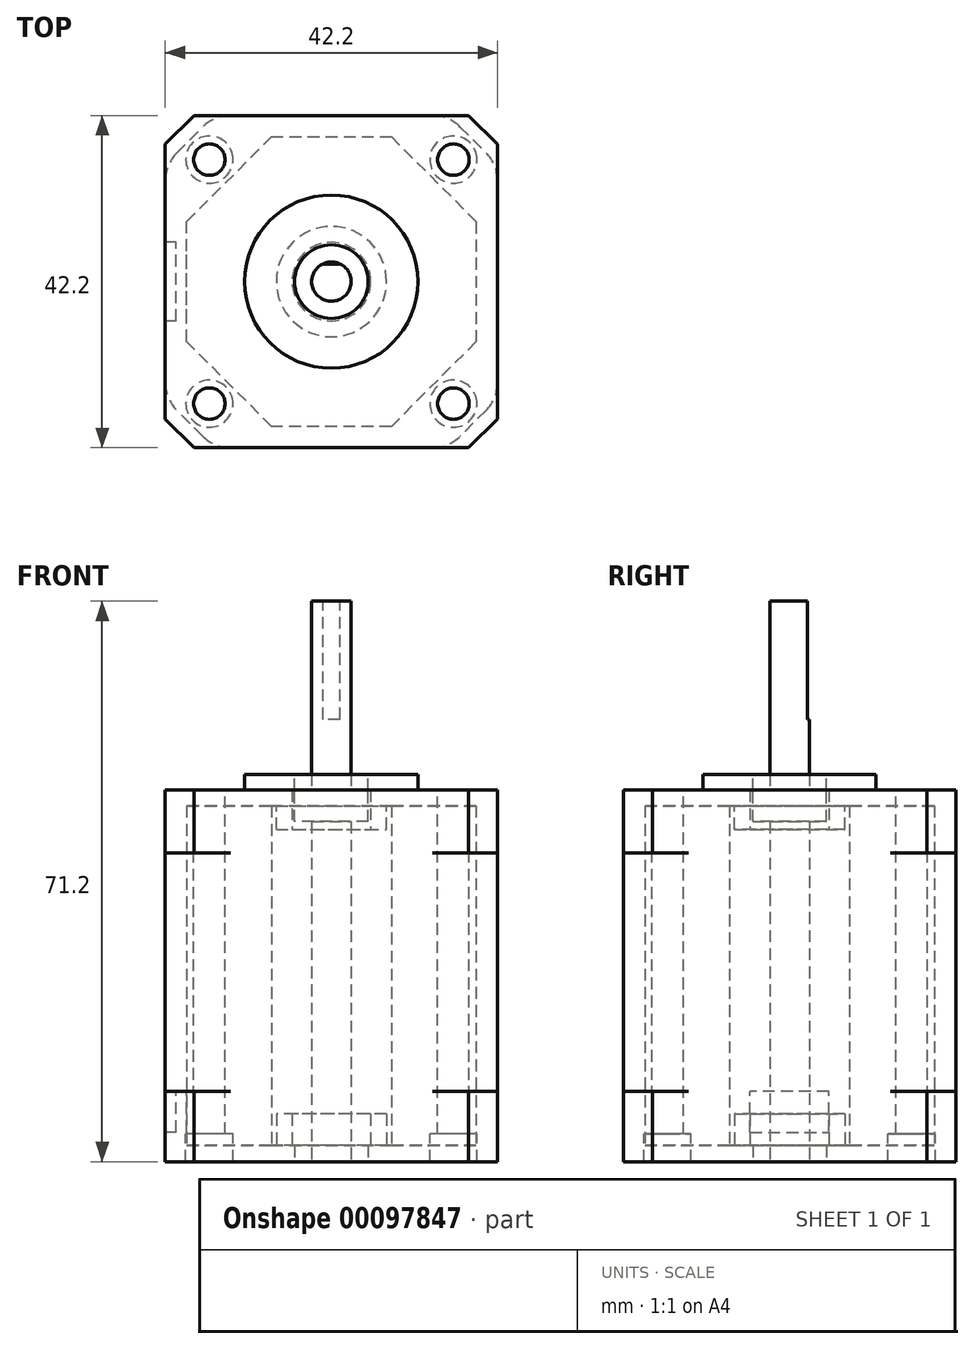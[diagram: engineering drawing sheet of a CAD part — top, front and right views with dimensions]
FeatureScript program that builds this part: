
annotation { "Feature Type Name" : "Feature", "Feature Type Description" : "" }
export const myFeature = defineFeature(function(context is Context, id is Id, definition is map)
    precondition{}
    {
        {
            var Q0;
            Q0=qCreatedBy(makeId("Top.planeOp"),FACE);
            var sketch = newSketch(context, id + "F0", { "sketchPlane" : qUnion([Q0])});
            skLineSegment(sketch, "E0.bottom", {"start": v(17.44, 21.1) * mm, "end": v(-17.44, 21.1) * mm});
            skLineSegment(sketch, "E0.top", {"start": v(17.44, -21.1) * mm, "end": v(-17.44, -21.1) * mm});
            skLineSegment(sketch, "E0.left", {"start": v(21.1, 17.44) * mm, "end": v(21.1, -17.44) * mm});
            skLineSegment(sketch, "E0.right", {"start": v(-21.1, 17.44) * mm, "end": v(-21.1, -17.44) * mm});
            skPoint(sketch, "E0.middle", {"position": v(0, 0) * mm});
            skLineSegment(sketch, "E1.bottom", {"start": v(15.5, 15.5) * mm, "end": v(-15.5, 15.5) * mm, "construction": true});
            skLineSegment(sketch, "E1.top", {"start": v(15.5, -15.5) * mm, "end": v(-15.5, -15.5) * mm, "construction": true});
            skLineSegment(sketch, "E1.left", {"start": v(15.5, 15.5) * mm, "end": v(15.5, -15.5) * mm, "construction": true});
            skLineSegment(sketch, "E1.right", {"start": v(-15.5, 15.5) * mm, "end": v(-15.5, -15.5) * mm, "construction": true});
            skCircle(sketch, "E2", {"center": v(-15.5, 15.5) * mm, "radius": 2 * mm});
            skCircle(sketch, "E3", {"center": v(15.5, 15.5) * mm, "radius": 2 * mm});
            skCircle(sketch, "E4", {"center": v(-15.5, -15.5) * mm, "radius": 2 * mm});
            skCircle(sketch, "E5", {"center": v(15.5, -15.5) * mm, "radius": 2 * mm});
            skLineSegment(sketch, "E6.1", {"start": v(-21.1, 17.44) * mm, "end": v(-17.44, 21.1) * mm});
            skLineSegment(sketch, "E7", {"start": v(0, 21.1) * mm, "end": v(0, -21.1) * mm, "construction": true});
            skLineSegment(sketch, "E8", {"start": v(-21.1, 0) * mm, "end": v(21.1, 0) * mm, "construction": true});
            skLineSegment(sketch, "E9.MirrorCS", {"start": v(21.1, 17.44) * mm, "end": v(17.44, 21.1) * mm});
            skLineSegment(sketch, "E10.MirrorCS", {"start": v(-21.1, -17.44) * mm, "end": v(-17.44, -21.1) * mm});
            skLineSegment(sketch, "E11.MirrorCS", {"start": v(21.1, -17.44) * mm, "end": v(17.44, -21.1) * mm});
            skCircle(sketch, "E12", {"center": v(0, 0) * mm, "radius": 4.68 * mm});
            skCircle(sketch, "E13", {"center": v(0, 0) * mm, "radius": 2.5 * mm});
            skCircle(sketch, "E14", {"center": v(0, 0) * mm, "radius": 11 * mm});
            skSolve(sketch);
        }
        {
            var Q0;
            Q0=makeQuery(id+"F0.imprint","IMPRINT",FACE,{"disambiguationData":[TD([[makeQuery(id+"F0.imprint","IMPRINT",EDGE,{"derivedFrom":sQuery(id+"F0.wireOp",EDGE,"E0.bottom")}),1.0]])]});
            var Q1;
            Q1=makeQuery(id+"F0.imprint","IMPRINT",FACE,{"disambiguationData":[TD([[makeQuery(id+"F0.imprint","IMPRINT",EDGE,{"derivedFrom":sQuery(id+"F0.wireOp",EDGE,"E12")}),-1.0]])]});
            extrude(context, id + "F1", {"entities" : qUnion([Q0, Q1]), "oppositeDirection" : true, "depth" : 8 * mm});
        }
        {
            var Q0;
            Q0=makeQuery(id+"F0.imprint","IMPRINT",FACE,{"disambiguationData":[TD([[makeQuery(id+"F0.imprint","IMPRINT",EDGE,{"derivedFrom":sQuery(id+"F0.wireOp",EDGE,"E12")}),-1.0]])]});
            extrude(context, id + "F2", {"entities" : qUnion([Q0]), "operationType" : NewBodyOperationType.ADD, "depth" : 2 * mm});
        }
        {
            var Q0;
            Q0=makeQuery(id+"F1.opExtrude","CAP_FACE",FACE,{"disambiguationData":[OSD([sQuery(id+"F0.wireOp",EDGE,"E0.bottom"),sQuery(id+"F0.wireOp",EDGE,"E0.top"),sQuery(id+"F0.wireOp",EDGE,"E0.left"),sQuery(id+"F0.wireOp",EDGE,"E0.right"),sQuery(id+"F0.wireOp",EDGE,"E2"),sQuery(id+"F0.wireOp",EDGE,"E3"),sQuery(id+"F0.wireOp",EDGE,"E4"),sQuery(id+"F0.wireOp",EDGE,"E5"),sQuery(id+"F0.wireOp",EDGE,"E6.1"),sQuery(id+"F0.wireOp",EDGE,"E9.MirrorCS"),sQuery(id+"F0.wireOp",EDGE,"E10.MirrorCS"),sQuery(id+"F0.wireOp",EDGE,"E11.MirrorCS"),sQuery(id+"F0.wireOp",EDGE,"E12")])],"isStart":true});
            cPlane(context, id + "F3", {"entities" : qUnion([Q0]), "cplaneType" : CPlaneType.OFFSET, "offset" : (47.2 - 3.5) * mm, "oppositeDirection" : true, "width" : 150 * mm, "height" : 150 * mm});
        }
        {
            var Q0;
            Q0=qCreatedBy(id+"F3.planeOp",FACE);
            var sketch = newSketch(context, id + "F4", { "sketchPlane" : qUnion([Q0])});
            skLineSegment(sketch, "E15.0", {"start": v(17.44, 21.1) * mm, "end": v(-17.44, 21.1) * mm});
            skLineSegment(sketch, "E15.1", {"start": v(17.44, -21.1) * mm, "end": v(-17.44, -21.1) * mm});
            skLineSegment(sketch, "E15.2", {"start": v(21.1, 17.44) * mm, "end": v(21.1, -17.44) * mm});
            skLineSegment(sketch, "E15.3", {"start": v(-21.1, 17.44) * mm, "end": v(-21.1, -17.44) * mm});
            skPoint(sketch, "E15.4", {"position": v(0, 0) * mm});
            skLineSegment(sketch, "E15.5", {"start": v(15.5, 15.5) * mm, "end": v(-15.5, 15.5) * mm, "construction": true});
            skLineSegment(sketch, "E15.6", {"start": v(15.5, -15.5) * mm, "end": v(-15.5, -15.5) * mm, "construction": true});
            skLineSegment(sketch, "E15.7", {"start": v(15.5, 15.5) * mm, "end": v(15.5, -15.5) * mm, "construction": true});
            skLineSegment(sketch, "E15.8", {"start": v(-15.5, 15.5) * mm, "end": v(-15.5, -15.5) * mm, "construction": true});
            skPoint(sketch, "E15.9", {"position": v(0, 0) * mm});
            skCircle(sketch, "E15.10", {"center": v(-15.5, 15.5) * mm, "radius": 2 * mm});
            skCircle(sketch, "E15.11", {"center": v(15.5, 15.5) * mm, "radius": 2 * mm});
            skCircle(sketch, "E15.12", {"center": v(-15.5, -15.5) * mm, "radius": 2 * mm});
            skCircle(sketch, "E15.13", {"center": v(15.5, -15.5) * mm, "radius": 2 * mm});
            skLineSegment(sketch, "E15.14", {"start": v(-21.1, 17.44) * mm, "end": v(-17.44, 21.1) * mm});
            skLineSegment(sketch, "E15.15", {"start": v(0, 21.1) * mm, "end": v(0, -21.1) * mm, "construction": true});
            skLineSegment(sketch, "E15.16", {"start": v(-21.1, 0) * mm, "end": v(21.1, 0) * mm, "construction": true});
            skLineSegment(sketch, "E15.17", {"start": v(21.1, 17.44) * mm, "end": v(17.44, 21.1) * mm});
            skLineSegment(sketch, "E15.18", {"start": v(-21.1, -17.44) * mm, "end": v(-17.44, -21.1) * mm});
            skLineSegment(sketch, "E15.19", {"start": v(21.1, -17.44) * mm, "end": v(17.44, -21.1) * mm});
            skCircle(sketch, "E15.20", {"center": v(0, 0) * mm, "radius": 4.68 * mm});
            skCircle(sketch, "E15.21", {"center": v(0, 0) * mm, "radius": 2.5 * mm});
            skCircle(sketch, "E16", {"center": v(15.5, 15.5) * mm, "radius": 3 * mm});
            skCircle(sketch, "E17.MirrorC", {"center": v(-15.5, 15.5) * mm, "radius": 3 * mm});
            skCircle(sketch, "E18.MirrorC", {"center": v(-15.5, -15.5) * mm, "radius": 3 * mm});
            skCircle(sketch, "E19.MirrorC", {"center": v(15.5, -15.5) * mm, "radius": 3 * mm});
            skSolve(sketch);
        }
        {
            var Q0;
            Q0=makeQuery(id+"F4.imprint","IMPRINT",FACE,{"disambiguationData":[TD([[makeQuery(id+"F4.imprint","IMPRINT",EDGE,{"derivedFrom":sQuery(id+"F4.wireOp",EDGE,"E15.0")}),1.0]])]});
            var Q1;
            Q1=makeQuery(id+"F4.imprint","IMPRINT",FACE,{"disambiguationData":[TD([[makeQuery(id+"F4.imprint","IMPRINT",EDGE,{"derivedFrom":sQuery(id+"F4.wireOp",EDGE,"E15.11")}),-1.0]])]});
            var Q2;
            Q2=makeQuery(id+"F4.imprint","IMPRINT",FACE,{"disambiguationData":[TD([[makeQuery(id+"F4.imprint","IMPRINT",EDGE,{"derivedFrom":sQuery(id+"F4.wireOp",EDGE,"E15.10")}),-1.0]])]});
            var Q3;
            Q3=makeQuery(id+"F4.imprint","IMPRINT",FACE,{"disambiguationData":[TD([[makeQuery(id+"F4.imprint","IMPRINT",EDGE,{"derivedFrom":sQuery(id+"F4.wireOp",EDGE,"E15.12")}),-1.0]])]});
            var Q4;
            Q4=makeQuery(id+"F4.imprint","IMPRINT",FACE,{"disambiguationData":[TD([[makeQuery(id+"F4.imprint","IMPRINT",EDGE,{"derivedFrom":sQuery(id+"F4.wireOp",EDGE,"E15.13")}),-1.0]])]});
            extrude(context, id + "F5", {"entities" : qUnion([Q0, Q1, Q2, Q3, Q4]), "depth" : (8.9 - 3.5) * mm});
        }
        {
            var Q0;
            Q0=makeQuery(id+"F4.imprint","IMPRINT",FACE,{"disambiguationData":[TD([[makeQuery(id+"F4.imprint","IMPRINT",EDGE,{"derivedFrom":sQuery(id+"F4.wireOp",EDGE,"E15.0")}),1.0]])]});
            extrude(context, id + "F6", {"entities" : qUnion([Q0]), "operationType" : NewBodyOperationType.ADD, "oppositeDirection" : true, "depth" : 3.5 * mm});
        }
        {
            var Q0;
            Q0=makeQuery(id+"F5.opExtrude","CAP_FACE",FACE,{"disambiguationData":[OSD([sQuery(id+"F4.wireOp",EDGE,"E15.0"),sQuery(id+"F4.wireOp",EDGE,"E15.1"),sQuery(id+"F4.wireOp",EDGE,"E15.2"),sQuery(id+"F4.wireOp",EDGE,"E15.3"),sQuery(id+"F4.wireOp",EDGE,"E15.10"),sQuery(id+"F4.wireOp",EDGE,"E15.11"),sQuery(id+"F4.wireOp",EDGE,"E15.12"),sQuery(id+"F4.wireOp",EDGE,"E15.13"),sQuery(id+"F4.wireOp",EDGE,"E15.14"),sQuery(id+"F4.wireOp",EDGE,"E15.17"),sQuery(id+"F4.wireOp",EDGE,"E15.18"),sQuery(id+"F4.wireOp",EDGE,"E15.19"),sQuery(id+"F4.wireOp",EDGE,"E15.20")])],"isStart":false});
            var sketch = newSketch(context, id + "F7", { "sketchPlane" : qUnion([Q0])});
            skLineSegment(sketch, "E20.1", {"start": v(16.7, -19.3) * mm, "end": v(19.3, -16.7) * mm});
            skLineSegment(sketch, "E20.2", {"start": v(19.3, 16.7) * mm, "end": v(16.7, 19.3) * mm});
            skLineSegment(sketch, "E20.5", {"start": v(-16.69, 19.3) * mm, "end": v(-19.3, 16.7) * mm});
            skLineSegment(sketch, "E20.7", {"start": v(-19.3, -16.7) * mm, "end": v(-16.7, -19.3) * mm});
            skLineSegment(sketch, "E21.0", {"start": v(-19.64, 16.36) * mm, "end": v(-19.3, 16.7) * mm});
            skLineSegment(sketch, "E21.2", {"start": v(16.36, 19.64) * mm, "end": v(16.7, 19.3) * mm});
            skLineSegment(sketch, "E21.4", {"start": v(19.64, -16.36) * mm, "end": v(19.3, -16.7) * mm});
            skLineSegment(sketch, "E21.6", {"start": v(-16.36, -19.64) * mm, "end": v(-19.64, -16.36) * mm});
            skLineSegment(sketch, "E22.0", {"start": v(-21.1, 12.82) * mm, "end": v(-21.1, -12.82) * mm});
            skLineSegment(sketch, "E22.1", {"start": v(-21.1, 17.44) * mm, "end": v(-17.44, 21.1) * mm});
            skLineSegment(sketch, "E22.2", {"start": v(12.82, 21.1) * mm, "end": v(-12.82, 21.1) * mm});
            skLineSegment(sketch, "E22.3", {"start": v(21.1, 17.44) * mm, "end": v(17.44, 21.1) * mm});
            skLineSegment(sketch, "E22.4", {"start": v(21.1, 12.82) * mm, "end": v(21.1, -12.82) * mm});
            skLineSegment(sketch, "E22.5", {"start": v(21.1, -17.44) * mm, "end": v(17.44, -21.1) * mm});
            skLineSegment(sketch, "E22.6", {"start": v(12.82, -21.1) * mm, "end": v(-12.82, -21.1) * mm});
            skLineSegment(sketch, "E22.7", {"start": v(-21.1, -17.44) * mm, "end": v(-17.44, -21.1) * mm});
            skPoint(sketch, "E23.orphan", {"position": v(-10.54, 25.45) * mm});
            skLineSegment(sketch, "E24.trimOffspring", {"start": v(16.7, -19.3) * mm, "end": v(16.36, -19.64) * mm});
            skLineSegment(sketch, "E25.trimOffspring", {"start": v(19.3, 16.7) * mm, "end": v(19.64, 16.36) * mm});
            skLineSegment(sketch, "E26.trimOffspring", {"start": v(-16.69, 19.3) * mm, "end": v(-16.36, 19.64) * mm});
            skCircle(sketch, "E27.cCircle", {"center": v(0, 0) * mm, "radius": 18.4 * mm, "construction": true});
            skLineSegment(sketch, "E27.0", {"start": v(-18.4, 7.61) * mm, "end": v(-7.62, 18.39) * mm});
            skLineSegment(sketch, "E27.1", {"start": v(-7.62, 18.39) * mm, "end": v(7.61, 18.4) * mm});
            skLineSegment(sketch, "E27.2", {"start": v(7.61, 18.4) * mm, "end": v(18.39, 7.62) * mm});
            skLineSegment(sketch, "E27.3", {"start": v(18.39, 7.62) * mm, "end": v(18.4, -7.61) * mm});
            skLineSegment(sketch, "E27.4", {"start": v(18.4, -7.61) * mm, "end": v(7.62, -18.39) * mm});
            skLineSegment(sketch, "E27.5", {"start": v(7.62, -18.39) * mm, "end": v(-7.61, -18.4) * mm});
            skLineSegment(sketch, "E27.6", {"start": v(-7.61, -18.4) * mm, "end": v(-18.39, -7.62) * mm});
            skLineSegment(sketch, "E27.7", {"start": v(-18.39, -7.62) * mm, "end": v(-18.4, 7.61) * mm});
            skLineSegment(sketch, "E28", {"start": v(0, 21.1) * mm, "end": v(0, -21.1) * mm, "construction": true});
            skPoint(sketch, "E29.newPointA", {"position": v(17.44, 21.1) * mm});
            skArc(sketch, "E29.filletArc", {"start": v(16.36, 19.64) * mm, "mid": v(14.73, 20.72) * mm, "end": v(12.82, 21.1) * mm});
            skArc(sketch, "E30.filletArc", {"start": v(21.1, 12.82) * mm, "mid": v(20.72, 14.73) * mm, "end": v(19.64, 16.36) * mm});
            skPoint(sketch, "E31.newPointB", {"position": v(-21.1, 17.44) * mm});
            skArc(sketch, "E31.filletArc", {"start": v(-19.64, 16.36) * mm, "mid": v(-20.72, 14.73) * mm, "end": v(-21.1, 12.82) * mm});
            skPoint(sketch, "E32.newPointB", {"position": v(-17.44, 21.1) * mm});
            skArc(sketch, "E32.filletArc", {"start": v(-12.82, 21.1) * mm, "mid": v(-14.73, 20.72) * mm, "end": v(-16.36, 19.64) * mm});
            skPoint(sketch, "E33.newPointB", {"position": v(21.1, -17.44) * mm});
            skArc(sketch, "E33.filletArc", {"start": v(19.64, -16.36) * mm, "mid": v(20.72, -14.73) * mm, "end": v(21.1, -12.82) * mm});
            skArc(sketch, "E34.filletArc", {"start": v(12.82, -21.1) * mm, "mid": v(14.73, -20.72) * mm, "end": v(16.36, -19.64) * mm});
            skPoint(sketch, "E35.newPointA", {"position": v(-21.1, -17.44) * mm});
            skArc(sketch, "E35.filletArc", {"start": v(-21.1, -12.82) * mm, "mid": v(-20.72, -14.73) * mm, "end": v(-19.64, -16.36) * mm});
            skPoint(sketch, "E36.newPointB", {"position": v(-17.44, -21.1) * mm});
            skArc(sketch, "E36.filletArc", {"start": v(-16.36, -19.64) * mm, "mid": v(-14.73, -20.72) * mm, "end": v(-12.82, -21.1) * mm});
            skPoint(sketch, "E37.middle", {"position": v(-18.4, 0) * mm});
            skSolve(sketch);
        }
        {
            var Q0;
            Q0=makeQuery(id+"F7.imprint","IMPRINT",FACE,{"disambiguationData":[TD([[makeQuery(id+"F7.imprint","IMPRINT",EDGE,{"derivedFrom":sQuery(id+"F7.wireOp",EDGE,"E20.1")}),1.0]])]});
            extrude(context, id + "F8", {"entities" : qUnion([Q0]), "endBound" : BoundingType.UP_TO_NEXT, "depth" : 25 * mm});
        }
        {
            var Q0;
            Q0=makeQuery(id+"F0.imprint","IMPRINT",FACE,{"disambiguationData":[TD([[makeQuery(id+"F0.imprint","IMPRINT",EDGE,{"derivedFrom":sQuery(id+"F0.wireOp",EDGE,"E13")}),1.0]])]});
            extrude(context, id + "F9", {"entities" : qUnion([Q0]), "depth" : 24 * mm});
        }
        {
            var Q0;
            Q0=makeQuery(id+"F0.imprint","IMPRINT",FACE,{"disambiguationData":[TD([[makeQuery(id+"F0.imprint","IMPRINT",EDGE,{"derivedFrom":sQuery(id+"F0.wireOp",EDGE,"E13")}),1.0]])]});
            var Q1;
            Q1=makeQuery(id+"F6.opExtrude","CAP_FACE",FACE,{"disambiguationData":[OSD([sQuery(id+"F4.wireOp",EDGE,"E15.0"),sQuery(id+"F4.wireOp",EDGE,"E15.1"),sQuery(id+"F4.wireOp",EDGE,"E15.2"),sQuery(id+"F4.wireOp",EDGE,"E15.3"),sQuery(id+"F4.wireOp",EDGE,"E15.14"),sQuery(id+"F4.wireOp",EDGE,"E15.17"),sQuery(id+"F4.wireOp",EDGE,"E15.18"),sQuery(id+"F4.wireOp",EDGE,"E15.19"),sQuery(id+"F4.wireOp",EDGE,"E15.20"),sQuery(id+"F4.wireOp",EDGE,"E16"),sQuery(id+"F4.wireOp",EDGE,"E17.MirrorC"),sQuery(id+"F4.wireOp",EDGE,"E18.MirrorC"),sQuery(id+"F4.wireOp",EDGE,"E19.MirrorC")])],"isStart":false});
            extrude(context, id + "F10", {"entities" : qUnion([Q0]), "operationType" : NewBodyOperationType.ADD, "endBound" : BoundingType.UP_TO_SURFACE, "oppositeDirection" : true, "endBoundEntityFace" : qUnion([Q1]), "depth" : 25 * mm});
        }
        {
            var Q0;
            Q0=makeQuery(id+"F9.opExtrude","CAP_FACE",FACE,{"disambiguationData":[OSD([sQuery(id+"F0.wireOp",EDGE,"E13")])],"isStart":false});
            var sketch = newSketch(context, id + "F11", { "sketchPlane" : qUnion([Q0])});
            skLineSegment(sketch, "E38", {"start": v(0, 0) * mm, "end": v(0, 2.25) * mm, "construction": true});
            skLineSegment(sketch, "E39", {"start": v(0, 2.25) * mm, "end": v(-1.09, 2.25) * mm});
            skLineSegment(sketch, "E40.MirrorCS", {"start": v(0, 2.25) * mm, "end": v(1.09, 2.25) * mm});
            skCircle(sketch, "E41.0", {"center": v(0, 0) * mm, "radius": 2.5 * mm});
            skSolve(sketch);
        }
        {
            var Q0;
            {var subQ0=sQuery(id+"F11.wireOp",EDGE,"E39");Q0=makeQuery(id+"F11.imprint","IMPRINT",FACE,{"disambiguationData":[TD([[makeQuery(id+"F11.imprint","IMPRINT",EDGE,{"derivedFrom":subQ0}),-1.0]])]});}
            extrude(context, id + "F12", {"entities" : qUnion([Q0]), "operationType" : NewBodyOperationType.REMOVE, "oppositeDirection" : true, "depth" : 15 * mm});
        }
        {
            var Q0;
            Q0=makeQuery(id+"F7.imprint","IMPRINT",FACE,{"disambiguationData":[TD([[makeQuery(id+"F7.imprint","IMPRINT",EDGE,{"derivedFrom":sQuery(id+"F7.wireOp",EDGE,"E27.0")}),-1.0]])]});
            extrude(context, id + "F13", {"entities" : qUnion([Q0]), "operationType" : NewBodyOperationType.REMOVE, "oppositeDirection" : true, "depth" : (8.86 - 2) * mm});
        }
        {
            var Q0;
            Q0=makeQuery(id+"F1.opExtrude","CAP_FACE",FACE,{"disambiguationData":[OSD([sQuery(id+"F0.wireOp",EDGE,"E0.bottom"),sQuery(id+"F0.wireOp",EDGE,"E0.top"),sQuery(id+"F0.wireOp",EDGE,"E0.left"),sQuery(id+"F0.wireOp",EDGE,"E0.right"),sQuery(id+"F0.wireOp",EDGE,"E2"),sQuery(id+"F0.wireOp",EDGE,"E3"),sQuery(id+"F0.wireOp",EDGE,"E4"),sQuery(id+"F0.wireOp",EDGE,"E5"),sQuery(id+"F0.wireOp",EDGE,"E6.1"),sQuery(id+"F0.wireOp",EDGE,"E9.MirrorCS"),sQuery(id+"F0.wireOp",EDGE,"E10.MirrorCS"),sQuery(id+"F0.wireOp",EDGE,"E11.MirrorCS"),sQuery(id+"F0.wireOp",EDGE,"E12")])],"isStart":false});
            var sketch = newSketch(context, id + "F14", { "sketchPlane" : qUnion([Q0])});
            skLineSegment(sketch, "E42.0.0", {"start": v(-7.62, -18.39) * mm, "end": v(-18.4, -7.61) * mm});
            skLineSegment(sketch, "E42.0.1", {"start": v(-18.4, -7.61) * mm, "end": v(-18.39, 7.62) * mm});
            skLineSegment(sketch, "E42.0.2", {"start": v(-18.39, 7.62) * mm, "end": v(-7.61, 18.4) * mm});
            skLineSegment(sketch, "E42.0.3", {"start": v(-7.61, 18.4) * mm, "end": v(7.62, 18.39) * mm});
            skLineSegment(sketch, "E42.0.4", {"start": v(7.62, 18.39) * mm, "end": v(18.4, 7.61) * mm});
            skLineSegment(sketch, "E42.0.5", {"start": v(18.4, 7.61) * mm, "end": v(18.39, -7.62) * mm});
            skLineSegment(sketch, "E42.0.6", {"start": v(18.39, -7.62) * mm, "end": v(7.61, -18.4) * mm});
            skLineSegment(sketch, "E42.0.7", {"start": v(7.61, -18.4) * mm, "end": v(-7.62, -18.39) * mm});
            skSolve(sketch);
        }
        {
            var Q0;
            Q0=makeQuery(id+"F14.imprint","IMPRINT",FACE,{"disambiguationData":[TD([[makeQuery(id+"F14.imprint","IMPRINT",EDGE,{"derivedFrom":sQuery(id+"F14.wireOp",EDGE,"E42.0.0")}),-1.0]])]});
            extrude(context, id + "F15", {"entities" : qUnion([Q0]), "operationType" : NewBodyOperationType.REMOVE, "oppositeDirection" : true, "depth" : 6 * mm});
        }
        {
            var Q0;
            Q0=makeQuery(id+"F15.boolean.opBoolean","COPY",FACE,{"derivedFrom":makeQuery(id+"F15.opExtrude","CAP_FACE",FACE,{"disambiguationData":[OSD([sQuery(id+"F0.wireOp",EDGE,"E12"),sQuery(id+"F14.wireOp",EDGE,"E42.0.0"),sQuery(id+"F14.wireOp",EDGE,"E42.0.1"),sQuery(id+"F14.wireOp",EDGE,"E42.0.2"),sQuery(id+"F14.wireOp",EDGE,"E42.0.3"),sQuery(id+"F14.wireOp",EDGE,"E42.0.4"),sQuery(id+"F14.wireOp",EDGE,"E42.0.5"),sQuery(id+"F14.wireOp",EDGE,"E42.0.6"),sQuery(id+"F14.wireOp",EDGE,"E42.0.7")])],"isStart":false})});
            var sketch = newSketch(context, id + "F16", { "sketchPlane" : qUnion([Q0])});
            skCircle(sketch, "E43.0", {"center": v(0, 0) * mm, "radius": 4.68 * mm});
            skCircle(sketch, "E44", {"center": v(0, 0) * mm, "radius": 5 * mm});
            skCircle(sketch, "E45", {"center": v(0, 0) * mm, "radius": 7 * mm});
            skSolve(sketch);
        }
        {
            var Q0;
            Q0=makeQuery(id+"F16.imprint","IMPRINT",FACE,{"disambiguationData":[TD([[makeQuery(id+"F16.imprint","IMPRINT",EDGE,{"derivedFrom":sQuery(id+"F16.wireOp",EDGE,"E43.0")}),1.0]])]});
            extrude(context, id + "F17", {"entities" : qUnion([Q0]), "operationType" : NewBodyOperationType.REMOVE, "oppositeDirection" : true, "depth" : 2 * mm});
        }
        {
            var Q0;
            Q0=makeQuery(id+"F16.imprint","IMPRINT",FACE,{"disambiguationData":[TD([[makeQuery(id+"F16.imprint","IMPRINT",EDGE,{"derivedFrom":sQuery(id+"F16.wireOp",EDGE,"E44")}),-1.0]])]});
            var Q1;
            Q1=makeQuery(id+"F1.opExtrude","CAP_FACE",FACE,{"disambiguationData":[OSD([sQuery(id+"F0.wireOp",EDGE,"E0.bottom"),sQuery(id+"F0.wireOp",EDGE,"E0.top"),sQuery(id+"F0.wireOp",EDGE,"E0.left"),sQuery(id+"F0.wireOp",EDGE,"E0.right"),sQuery(id+"F0.wireOp",EDGE,"E2"),sQuery(id+"F0.wireOp",EDGE,"E3"),sQuery(id+"F0.wireOp",EDGE,"E4"),sQuery(id+"F0.wireOp",EDGE,"E5"),sQuery(id+"F0.wireOp",EDGE,"E6.1"),sQuery(id+"F0.wireOp",EDGE,"E9.MirrorCS"),sQuery(id+"F0.wireOp",EDGE,"E10.MirrorCS"),sQuery(id+"F0.wireOp",EDGE,"E11.MirrorCS"),sQuery(id+"F0.wireOp",EDGE,"E12")])],"isStart":false});
            extrude(context, id + "F18", {"entities" : qUnion([Q0]), "operationType" : NewBodyOperationType.ADD, "endBoundEntityFace" : qUnion([Q1]), "depth" : 3 * mm});
        }
        {
            var Q0;
            Q0=makeQuery(id+"F13.boolean.opBoolean","COPY",FACE,{"derivedFrom":makeQuery(id+"F13.opExtrude","CAP_FACE",FACE,{"disambiguationData":[OSD([sQuery(id+"F4.wireOp",EDGE,"E15.20"),sQuery(id+"F7.wireOp",EDGE,"E27.0"),sQuery(id+"F7.wireOp",EDGE,"E27.1"),sQuery(id+"F7.wireOp",EDGE,"E27.2"),sQuery(id+"F7.wireOp",EDGE,"E27.3"),sQuery(id+"F7.wireOp",EDGE,"E27.4"),sQuery(id+"F7.wireOp",EDGE,"E27.5"),sQuery(id+"F7.wireOp",EDGE,"E27.6"),sQuery(id+"F7.wireOp",EDGE,"E27.7")])],"isStart":false})});
            var sketch = newSketch(context, id + "F19", { "sketchPlane" : qUnion([Q0])});
            skCircle(sketch, "E46.0.0", {"center": v(0, 0) * mm, "radius": 7 * mm});
            skCircle(sketch, "E47.0", {"center": v(0, 0) * mm, "radius": 4.68 * mm});
            skCircle(sketch, "E47.1", {"center": v(0, 0) * mm, "radius": 5 * mm});
            skSolve(sketch);
        }
        {
            var Q0;
            Q0=makeQuery(id+"F19.imprint","IMPRINT",FACE,{"disambiguationData":[TD([[makeQuery(id+"F19.imprint","IMPRINT",EDGE,{"derivedFrom":sQuery(id+"F19.wireOp",EDGE,"E46.0.0")}),1.0]])]});
            var Q1;
            Q1=makeQuery(id+"F5.opExtrude","CAP_FACE",FACE,{"disambiguationData":[OSD([sQuery(id+"F4.wireOp",EDGE,"E15.0"),sQuery(id+"F4.wireOp",EDGE,"E15.1"),sQuery(id+"F4.wireOp",EDGE,"E15.2"),sQuery(id+"F4.wireOp",EDGE,"E15.3"),sQuery(id+"F4.wireOp",EDGE,"E15.10"),sQuery(id+"F4.wireOp",EDGE,"E15.11"),sQuery(id+"F4.wireOp",EDGE,"E15.12"),sQuery(id+"F4.wireOp",EDGE,"E15.13"),sQuery(id+"F4.wireOp",EDGE,"E15.14"),sQuery(id+"F4.wireOp",EDGE,"E15.17"),sQuery(id+"F4.wireOp",EDGE,"E15.18"),sQuery(id+"F4.wireOp",EDGE,"E15.19"),sQuery(id+"F4.wireOp",EDGE,"E15.20")])],"isStart":false});
            extrude(context, id + "F20", {"entities" : qUnion([Q0]), "operationType" : NewBodyOperationType.ADD, "endBoundEntityFace" : qUnion([Q1]), "depth" : 4 * mm});
        }
        {
            var Q0;
            Q0=makeQuery(id+"F17.boolean.opBoolean","COPY",FACE,{"derivedFrom":makeQuery(id+"F17.opExtrude","CAP_FACE",FACE,{"disambiguationData":[OSD([sQuery(id+"F16.wireOp",EDGE,"E43.0"),sQuery(id+"F16.wireOp",EDGE,"E44")])],"isStart":false})});
            var sketch = newSketch(context, id + "F21", { "sketchPlane" : qUnion([Q0])});
            skCircle(sketch, "E48", {"center": v(0, 0) * mm, "radius": 2.5 * mm});
            skCircle(sketch, "E49", {"center": v(0, 0) * mm, "radius": 5 * mm});
            skSolve(sketch);
        }
        {
            var Q0;
            Q0=makeQuery(id+"F21.imprint","IMPRINT",FACE,{"disambiguationData":[TD([[makeQuery(id+"F21.imprint","IMPRINT",EDGE,{"derivedFrom":sQuery(id+"F21.wireOp",EDGE,"E48")}),-1.0]])]});
            extrude(context, id + "F22", {"entities" : qUnion([Q0]), "depth" : 4 * mm});
        }
        {
            var Q0;
            {var subQ0=sQuery(id+"F4.wireOp",EDGE,"E15.3");Q0=makeQuery(id+"F6.boolean.opBoolean","MERGE",FACE,{"derivedFrom":[makeQuery(id+"F5.opExtrude","SWEPT_FACE",FACE,{"disambiguationData":[OSD([subQ0])]}),makeQuery(id+"F6.opExtrude","SWEPT_FACE",FACE,{"disambiguationData":[OSD([subQ0])]})]});}
            var sketch = newSketch(context, id + "F23", { "sketchPlane" : qUnion([Q0])});
            skLineSegment(sketch, "E50.bottom", {"start": v(5, -43.46) * mm, "end": v(-5, -43.46) * mm});
            skLineSegment(sketch, "E50.left", {"start": v(5, -43.46) * mm, "end": v(5, -38.3) * mm});
            skLineSegment(sketch, "E50.right", {"start": v(-5, -43.46) * mm, "end": v(-5, -38.3) * mm});
            skPoint(sketch, "E50.middle", {"position": v(0, -38.3) * mm});
            skSolve(sketch);
        }
        {
            var Q0;
            Q0=makeQuery(id+"F23.imprint","IMPRINT",FACE,{"disambiguationData":[TD([[makeQuery(id+"F23.imprint","IMPRINT",EDGE,{"derivedFrom":sQuery(id+"F23.wireOp",EDGE,"E50.bottom")}),-1.0]])]});
            extrude(context, id + "F24", {"entities" : qUnion([Q0]), "operationType" : NewBodyOperationType.REMOVE, "endBound" : BoundingType.UP_TO_NEXT, "oppositeDirection" : true, "depth" : 25 * mm});
        }
        {
            var Q0;
            Q0=makeQuery(id+"F24.boolean.opBoolean","COPY",FACE,{"derivedFrom":makeQuery(id+"F24.opExtrude","SWEPT_FACE",FACE,{"disambiguationData":[OSD([sQuery(id+"F23.wireOp",EDGE,"E50.right")])]})});
            var sketch = newSketch(context, id + "F25", { "sketchPlane" : qUnion([Q0])});
            skLineSegment(sketch, "E51.bottom", {"start": v(-18.4, -43.46) * mm, "end": v(-19.75, -43.46) * mm});
            skLineSegment(sketch, "E51.top", {"start": v(-18.4, -38.3) * mm, "end": v(-19.75, -38.3) * mm});
            skLineSegment(sketch, "E51.left", {"start": v(-18.4, -43.46) * mm, "end": v(-18.4, -38.3) * mm});
            skLineSegment(sketch, "E51.right", {"start": v(-19.75, -43.46) * mm, "end": v(-19.75, -38.3) * mm});
            skSolve(sketch);
        }
        {
            var Q0;
            Q0=makeQuery(id+"F25.imprint","IMPRINT",FACE,{"disambiguationData":[TD([[makeQuery(id+"F25.imprint","IMPRINT",EDGE,{"derivedFrom":sQuery(id+"F25.wireOp",EDGE,"E51.bottom")}),-1.0]])]});
            var Q1;
            Q1=makeQuery(id+"F24.boolean.opBoolean","COPY",FACE,{"derivedFrom":makeQuery(id+"F24.opExtrude","SWEPT_FACE",FACE,{"disambiguationData":[OSD([sQuery(id+"F23.wireOp",EDGE,"E50.left")])]})});
            extrude(context, id + "F26", {"entities" : qUnion([Q0]), "endBound" : BoundingType.UP_TO_SURFACE, "endBoundEntityFace" : qUnion([Q1]), "depth" : 25 * mm});
        }
        {
            var Q0;
            Q0=makeQuery(id+"F1.opExtrude","SWEPT_BODY",BODY,{"disambiguationData":[OSD([sQuery(id+"F0.wireOp",EDGE,"E0.bottom"),sQuery(id+"F0.wireOp",EDGE,"E0.top"),sQuery(id+"F0.wireOp",EDGE,"E0.left"),sQuery(id+"F0.wireOp",EDGE,"E0.right"),sQuery(id+"F0.wireOp",EDGE,"E2"),sQuery(id+"F0.wireOp",EDGE,"E3"),sQuery(id+"F0.wireOp",EDGE,"E4"),sQuery(id+"F0.wireOp",EDGE,"E5"),sQuery(id+"F0.wireOp",EDGE,"E6.1"),sQuery(id+"F0.wireOp",EDGE,"E9.MirrorCS"),sQuery(id+"F0.wireOp",EDGE,"E10.MirrorCS"),sQuery(id+"F0.wireOp",EDGE,"E11.MirrorCS"),sQuery(id+"F0.wireOp",EDGE,"E12")])]});
            var Q1;
            Q1=makeQuery(id+"F5.opExtrude","SWEPT_BODY",BODY,{"disambiguationData":[OSD([sQuery(id+"F4.wireOp",EDGE,"E15.0"),sQuery(id+"F4.wireOp",EDGE,"E15.1"),sQuery(id+"F4.wireOp",EDGE,"E15.2"),sQuery(id+"F4.wireOp",EDGE,"E15.3"),sQuery(id+"F4.wireOp",EDGE,"E15.10"),sQuery(id+"F4.wireOp",EDGE,"E15.11"),sQuery(id+"F4.wireOp",EDGE,"E15.12"),sQuery(id+"F4.wireOp",EDGE,"E15.13"),sQuery(id+"F4.wireOp",EDGE,"E15.14"),sQuery(id+"F4.wireOp",EDGE,"E15.17"),sQuery(id+"F4.wireOp",EDGE,"E15.18"),sQuery(id+"F4.wireOp",EDGE,"E15.19"),sQuery(id+"F4.wireOp",EDGE,"E15.20")])]});
            var Q2;
            Q2=makeQuery(id+"F8.opExtrude","SWEPT_BODY",BODY,{"disambiguationData":[OSD([sQuery(id+"F4.wireOp",EDGE,"E15.10"),sQuery(id+"F4.wireOp",EDGE,"E15.11"),sQuery(id+"F4.wireOp",EDGE,"E15.12"),sQuery(id+"F4.wireOp",EDGE,"E15.13"),sQuery(id+"F7.wireOp",EDGE,"E20.1"),sQuery(id+"F7.wireOp",EDGE,"E20.2"),sQuery(id+"F7.wireOp",EDGE,"E20.5"),sQuery(id+"F7.wireOp",EDGE,"E21.0"),sQuery(id+"F7.wireOp",EDGE,"E21.2"),sQuery(id+"F7.wireOp",EDGE,"E21.4"),sQuery(id+"F7.wireOp",EDGE,"E21.6"),sQuery(id+"F7.wireOp",EDGE,"E22.0"),sQuery(id+"F7.wireOp",EDGE,"E22.2"),sQuery(id+"F7.wireOp",EDGE,"E22.4"),sQuery(id+"F7.wireOp",EDGE,"E22.6"),sQuery(id+"F7.wireOp",EDGE,"E24.trimOffspring"),sQuery(id+"F7.wireOp",EDGE,"E25.trimOffspring"),sQuery(id+"F7.wireOp",EDGE,"E26.trimOffspring"),sQuery(id+"F7.wireOp",EDGE,"E27.0"),sQuery(id+"F7.wireOp",EDGE,"E27.1"),sQuery(id+"F7.wireOp",EDGE,"E27.2"),sQuery(id+"F7.wireOp",EDGE,"E27.3"),sQuery(id+"F7.wireOp",EDGE,"E27.4"),sQuery(id+"F7.wireOp",EDGE,"E27.5"),sQuery(id+"F7.wireOp",EDGE,"E27.6"),sQuery(id+"F7.wireOp",EDGE,"E27.7"),sQuery(id+"F7.wireOp",EDGE,"E29.filletArc"),sQuery(id+"F7.wireOp",EDGE,"E30.filletArc"),sQuery(id+"F7.wireOp",EDGE,"E31.filletArc"),sQuery(id+"F7.wireOp",EDGE,"E32.filletArc"),sQuery(id+"F7.wireOp",EDGE,"E33.filletArc"),sQuery(id+"F7.wireOp",EDGE,"E34.filletArc"),sQuery(id+"F7.wireOp",EDGE,"E35.filletArc"),sQuery(id+"F7.wireOp",EDGE,"E36.filletArc")])]});
            var Q3;
            Q3=makeQuery(id+"F9.opExtrude","SWEPT_BODY",BODY,{"disambiguationData":[OSD([sQuery(id+"F0.wireOp",EDGE,"E13")])]});
            var Q4;
            Q4=makeQuery(id+"F22.opExtrude","SWEPT_BODY",BODY,{"disambiguationData":[OSD([sQuery(id+"F16.wireOp",EDGE,"E43.0"),sQuery(id+"F21.wireOp",EDGE,"E48")])]});
            var Q5;
            Q5=makeQuery(id+"F26.opExtrude","SWEPT_BODY",BODY,{"disambiguationData":[OSD([sQuery(id+"F25.wireOp",EDGE,"E51.bottom"),sQuery(id+"F25.wireOp",EDGE,"E51.top"),sQuery(id+"F25.wireOp",EDGE,"E51.left"),sQuery(id+"F25.wireOp",EDGE,"E51.right")])]});
            booleanBodies(context, id + "F27", {"operationType" : BooleanOperationType.UNION, "tools" : qUnion([Q0, Q1, Q2, Q3, Q4, Q5])});
        }
    });
